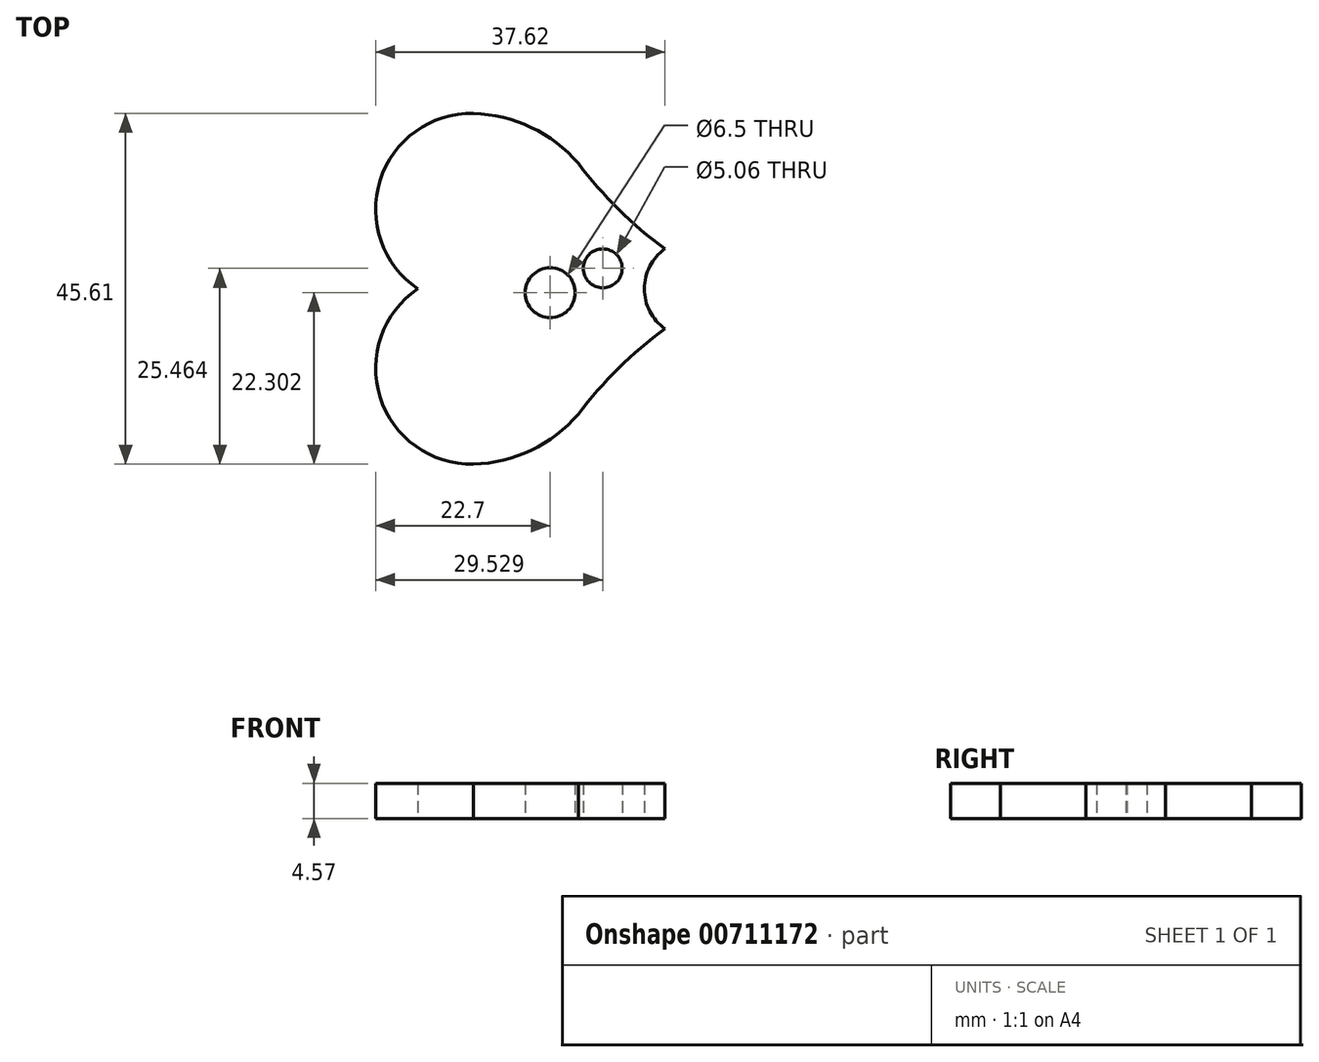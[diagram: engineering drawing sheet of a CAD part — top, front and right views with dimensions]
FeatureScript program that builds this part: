
annotation { "Feature Type Name" : "Feature", "Feature Type Description" : "" }
export const myFeature = defineFeature(function(context is Context, id is Id, definition is map)
    precondition{}
    {
        {
            var Q0;
            Q0=qCreatedBy(makeId("Top.planeOp"),FACE);
            var sketch = newSketch(context, id + "F0", { "sketchPlane" : qUnion([Q0])});
            skArc(sketch, "E0", {"start": v(12.64, 0) * mm, "mid": v(0.51, -8.7) * mm, "end": v(5.43, -22.8) * mm});
            skArc(sketch, "E1", {"start": v(26.3, -6.49) * mm, "mid": v(20.15, -1.81) * mm, "end": v(12.64, 0) * mm});
            skArc(sketch, "E2", {"start": v(26.3, -6.49) * mm, "mid": v(31.52, -12.46) * mm, "end": v(37.55, -17.62) * mm});
            skArc(sketch, "E3", {"start": v(37.55, -17.62) * mm, "mid": v(39.77, -20.11) * mm, "end": v(42.67, -21.8) * mm});
            skLineSegment(sketch, "E4", {"start": v(42.67, -21.8) * mm, "end": v(42.67, -22.8) * mm});
            skArc(sketch, "E5.MirrorCS", {"start": v(37.55, -27.99) * mm, "mid": v(39.77, -25.49) * mm, "end": v(42.67, -23.81) * mm});
            skArc(sketch, "E6.MirrorCS", {"start": v(26.3, -39.11) * mm, "mid": v(31.52, -33.14) * mm, "end": v(37.55, -27.99) * mm});
            skArc(sketch, "E7.MirrorCS", {"start": v(26.3, -39.11) * mm, "mid": v(20.15, -43.79) * mm, "end": v(12.64, -45.6) * mm});
            skArc(sketch, "E8.MirrorCS", {"start": v(12.64, -45.6) * mm, "mid": v(0.51, -36.9) * mm, "end": v(5.43, -22.8) * mm});
            skLineSegment(sketch, "E9", {"start": v(42.67, -23.81) * mm, "end": v(42.67, -22.8) * mm});
            skCircle(sketch, "E10", {"center": v(22.63, -23.3) * mm, "radius": 3.25 * mm});
            skCircle(sketch, "E11", {"center": v(29.46, -20.15) * mm, "radius": 2.53 * mm});
            skArc(sketch, "E12", {"start": v(37.55, -17.62) * mm, "mid": v(34.87, -22.8) * mm, "end": v(37.55, -27.99) * mm});
            skSolve(sketch);
        }
        {
            var Q0;
            Q0=makeQuery(id+"F0.imprint","IMPRINT",FACE,{"disambiguationData":[TD([[makeQuery(id+"F0.imprint","IMPRINT",EDGE,{"derivedFrom":sQuery(id+"F0.wireOp",EDGE,"E0")}),1.0]])]});
            extrude(context, id + "F1", {"entities" : qUnion([Q0]), "depth" : 4.57 * mm, "offsetDistance" : 25.4 * mm});
        }
    });
